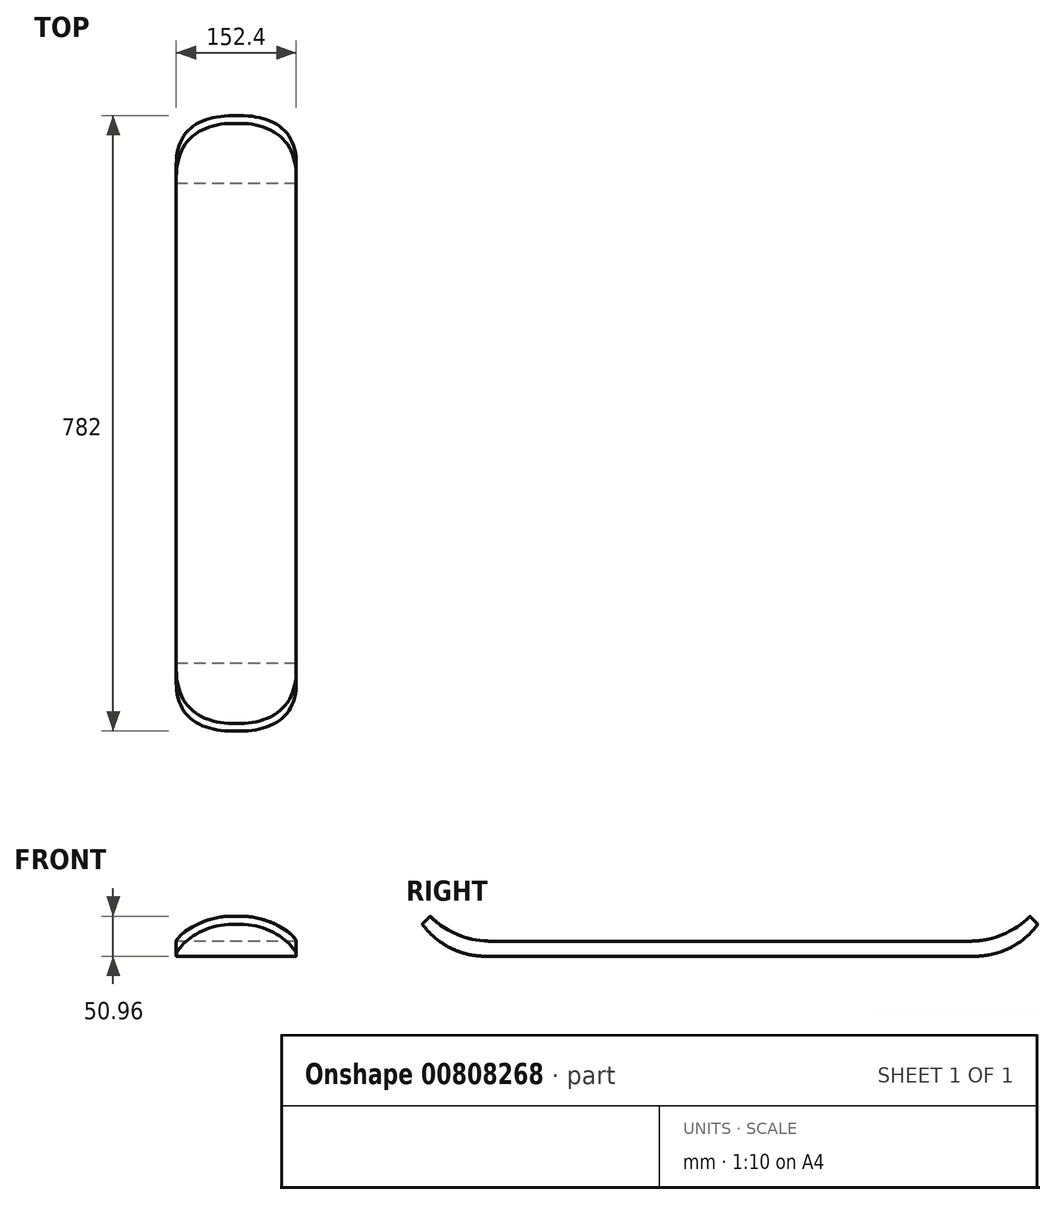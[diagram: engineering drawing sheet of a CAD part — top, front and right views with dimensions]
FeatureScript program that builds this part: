
annotation { "Feature Type Name" : "Feature", "Feature Type Description" : "" }
export const myFeature = defineFeature(function(context is Context, id is Id, definition is map)
    precondition{}
    {
        {
            var Q0;
            Q0=qCreatedBy(makeId("Right.planeOp"),FACE);
            var sketch = newSketch(context, id + "F0", { "sketchPlane" : qUnion([Q0])});
            skLineSegment(sketch, "E0", {"start": v(0, 0) * mm, "end": v(304.8, 0) * mm});
            skLineSegment(sketch, "E1", {"start": v(304.8, 19.05) * mm, "end": v(0, 19.05) * mm});
            skLineSegment(sketch, "E2", {"start": v(0, 19.05) * mm, "end": v(0, 0) * mm, "construction": true});
            skArc(sketch, "E3", {"start": v(304.8, 19.05) * mm, "mid": v(346.12, 27.3) * mm, "end": v(381.1, 50.8) * mm});
            skArc(sketch, "E4", {"start": v(304.8, 0) * mm, "mid": v(353.04, 9.36) * mm, "end": v(391, 40.58) * mm});
            skArc(sketch, "E5.MirrorCS", {"start": v(-304.8, 19.05) * mm, "mid": v(-346.12, 27.3) * mm, "end": v(-381.1, 50.8) * mm});
            skLineSegment(sketch, "E6.MirrorCS", {"start": v(-304.8, 19.05) * mm, "end": v(0, 19.05) * mm});
            skArc(sketch, "E7.MirrorCS", {"start": v(-304.8, 0) * mm, "mid": v(-353.04, 9.36) * mm, "end": v(-391, 40.58) * mm});
            skLineSegment(sketch, "E8.MirrorCS", {"start": v(0, 0) * mm, "end": v(-304.8, 0) * mm});
            skLineSegment(sketch, "E9", {"start": v(381.1, 50.8) * mm, "end": v(391, 40.58) * mm});
            skLineSegment(sketch, "E10", {"start": v(-391, 40.58) * mm, "end": v(-381.1, 50.8) * mm});
            skSolve(sketch);
        }
        {
            var Q0;
            Q0=makeQuery(id+"F0.imprint","IMPRINT",FACE,{"disambiguationData":[TD([[makeQuery(id+"F0.imprint","IMPRINT",EDGE,{"derivedFrom":sQuery(id+"F0.wireOp",EDGE,"E0")}),1.0]])]});
            extrude(context, id + "F1", {"entities" : qUnion([Q0]), "endBound" : BoundingType.SYMMETRIC, "depth" : 152.4 * mm, "offsetDistance" : 25.4 * mm});
        }
        {
            var Q0;
            Q0=makeQuery(id+"F1.opExtrude","CAP_EDGE",EDGE,{"disambiguationData":[OSD([sQuery(id+"F0.wireOp",EDGE,"E10")])],"isStart":false});
            var Q1;
            Q1=makeQuery(id+"F1.opExtrude","CAP_EDGE",EDGE,{"disambiguationData":[OSD([sQuery(id+"F0.wireOp",EDGE,"E10")])],"isStart":true});
            var Q2;
            Q2=makeQuery(id+"F1.opExtrude","CAP_EDGE",EDGE,{"disambiguationData":[OSD([sQuery(id+"F0.wireOp",EDGE,"E9")])],"isStart":false});
            var Q3;
            Q3=makeQuery(id+"F1.opExtrude","CAP_EDGE",EDGE,{"disambiguationData":[OSD([sQuery(id+"F0.wireOp",EDGE,"E9")])],"isStart":true});
            fillet(context, id + "F2", {"entities" : qUnion([Q0, Q1, Q2, Q3]), "radius" : 71.12 * mm, "tangentPropagation" : true, "allowEdgeOverflow" : false});
        }
    });
